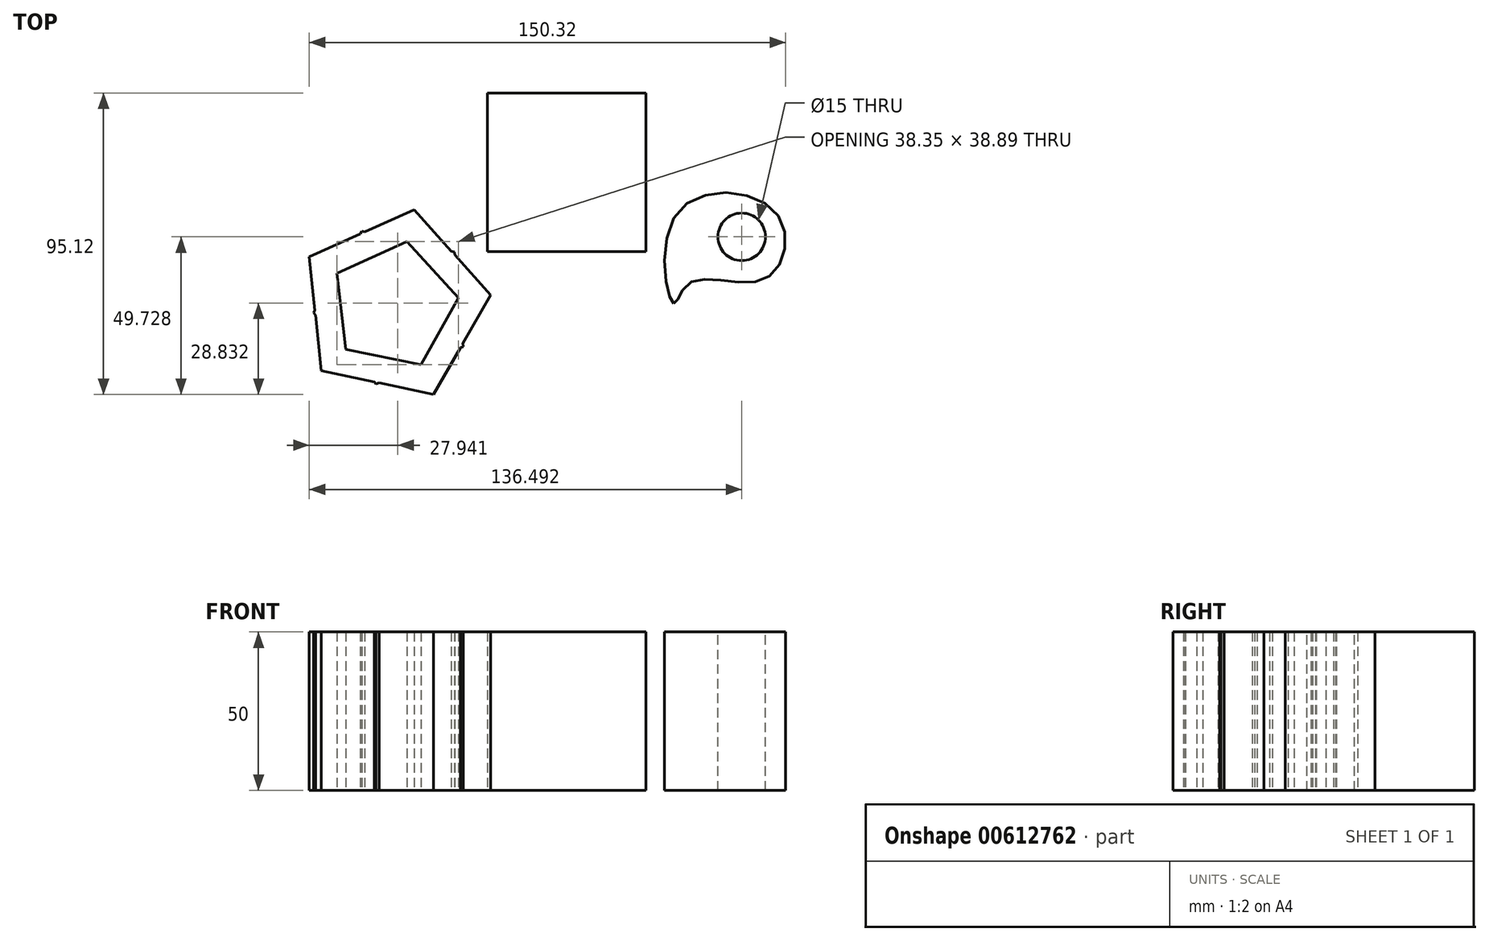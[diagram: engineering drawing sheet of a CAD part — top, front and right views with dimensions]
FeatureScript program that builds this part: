
annotation { "Feature Type Name" : "Feature", "Feature Type Description" : "" }
export const myFeature = defineFeature(function(context is Context, id is Id, definition is map)
    precondition{}
    {
        {
            var Q0;
            Q0=qCreatedBy(makeId("Top.planeOp"),FACE);
            var sketch = newSketch(context, id + "F0", { "sketchPlane" : qUnion([Q0])});
            skLineSegment(sketch, "E0.bottom", {"start": v(-25, -25) * mm, "end": v(25, -25) * mm});
            skLineSegment(sketch, "E0.top", {"start": v(-25, 25) * mm, "end": v(25, 25) * mm});
            skLineSegment(sketch, "E0.left", {"start": v(-25, -25) * mm, "end": v(-25, 25) * mm});
            skLineSegment(sketch, "E0.right", {"start": v(25, -25) * mm, "end": v(25, 25) * mm});
            skPoint(sketch, "E0.middle", {"position": v(0, 0) * mm});
            skSolve(sketch);
        }
        {
            var Q0;
            Q0 = qSketchRegion(id + "F0", true);
            extrude(context, id + "F1", {"entities" : qUnion([Q0]), "depth" : 50 * mm, "offsetDistance" : 25 * mm});
        }
        {
            var Q0;
            Q0=qCreatedBy(makeId("Top.planeOp"),FACE);
            var sketch = newSketch(context, id + "F2", { "sketchPlane" : qUnion([Q0])});
            skFitSpline(sketch, "E1", {"points": [v(33.74, -41.44) * mm, v(34.68, -13.06) * mm, v(66.06, -12.87) * mm, v(62.68, -33.55) * mm, v(38.81, -34.86) * mm, v(33.74, -41.44) * mm]});
            skCircle(sketch, "E2.cCircle", {"center": v(-54.6, -42) * mm, "radius": 24.9 * mm, "construction": true});
            skLineSegment(sketch, "E2.0", {"start": v(-81.27, -26.64) * mm, "end": v(-48.23, -11.9) * mm});
            skLineSegment(sketch, "E2.1", {"start": v(-48.23, -11.9) * mm, "end": v(-23.99, -38.76) * mm});
            skLineSegment(sketch, "E2.2", {"start": v(-23.99, -38.76) * mm, "end": v(-42.05, -70.12) * mm});
            skLineSegment(sketch, "E2.3", {"start": v(-42.05, -70.12) * mm, "end": v(-77.46, -62.62) * mm});
            skLineSegment(sketch, "E2.4", {"start": v(-77.46, -62.62) * mm, "end": v(-81.27, -26.64) * mm});
            skPoint(sketch, "E2.0.midPoint", {"position": v(-64.75, -19.26) * mm});
            skCircle(sketch, "E3.cCircle", {"center": v(-54.6, -42) * mm, "radius": 20.61 * mm, "construction": true});
            skLineSegment(sketch, "E3.0", {"start": v(-64.7, -18.62) * mm, "end": v(-35.48, -25.17) * mm});
            skLineSegment(sketch, "E3.1", {"start": v(-35.48, -25.17) * mm, "end": v(-32.68, -55) * mm});
            skLineSegment(sketch, "E3.2", {"start": v(-32.68, -55) * mm, "end": v(-60.17, -66.86) * mm});
            skLineSegment(sketch, "E3.3", {"start": v(-60.17, -66.86) * mm, "end": v(-79.96, -44.39) * mm});
            skLineSegment(sketch, "E3.4", {"start": v(-79.96, -44.39) * mm, "end": v(-64.7, -18.62) * mm});
            skPoint(sketch, "E3.0.midPoint", {"position": v(-50.09, -21.9) * mm});
            skCircle(sketch, "E4.cCircle", {"center": v(-54.6, -42) * mm, "radius": 16.65 * mm, "construction": true});
            skLineSegment(sketch, "E4.0", {"start": v(-69.77, -55.9) * mm, "end": v(-72.5, -31.87) * mm});
            skLineSegment(sketch, "E4.1", {"start": v(-72.5, -31.87) * mm, "end": v(-50.5, -21.85) * mm});
            skLineSegment(sketch, "E4.2", {"start": v(-50.5, -21.85) * mm, "end": v(-34.15, -39.68) * mm});
            skLineSegment(sketch, "E4.3", {"start": v(-34.15, -39.68) * mm, "end": v(-46.07, -60.73) * mm});
            skLineSegment(sketch, "E4.4", {"start": v(-46.07, -60.73) * mm, "end": v(-69.77, -55.9) * mm});
            skPoint(sketch, "E4.0.midPoint", {"position": v(-71.14, -43.89) * mm});
            skSolve(sketch);
        }
        {
            var Q0;
            Q0=makeQuery(id+"F2.imprint","IMPRINT",FACE,{"disambiguationData":[TD([[makeQuery(id+"F2.imprint","IMPRINT",EDGE,{"derivedFrom":sQuery(id+"F2.wireOp",EDGE,"E1")}),-1.0]])]});
            var Q1;
            {var subQ0=sQuery(id+"F2.wireOp",EDGE,"E2.4");var subQ1=sQuery(id+"F2.wireOp",EDGE,"E2.0");var subQ2=makeQuery(id+"F2.imprint","INTERSECT",VERTEX,{"derivedFrom":[subQ1,subQ0]});Q1=makeQuery(id+"F2.imprint","IMPRINT",FACE,{"disambiguationData":[TD([[makeQuery(id+"F2.imprint","IMPRINT",EDGE,{"disambiguationData":[TD([[subQ2,-1.0]])],"derivedFrom":subQ1}),-1.0]])]});}
            var Q2;
            {var subQ0=sQuery(id+"F2.wireOp",EDGE,"E3.4");var subQ1=sQuery(id+"F2.wireOp",EDGE,"E2.0");var subQ2=makeQuery(id+"F2.imprint","INTERSECT",VERTEX,{"derivedFrom":[subQ1,subQ0]});Q2=makeQuery(id+"F2.imprint","IMPRINT",FACE,{"disambiguationData":[TD([[makeQuery(id+"F2.imprint","IMPRINT",EDGE,{"disambiguationData":[TD([[subQ2,-1.0]])],"derivedFrom":subQ1}),1.0]])]});}
            var Q3;
            {var subQ0=sQuery(id+"F2.wireOp",EDGE,"E3.0");var subQ1=sQuery(id+"F2.wireOp",EDGE,"E2.1");var subQ2=makeQuery(id+"F2.imprint","INTERSECT",VERTEX,{"derivedFrom":[subQ1,subQ0]});Q3=makeQuery(id+"F2.imprint","IMPRINT",FACE,{"disambiguationData":[TD([[makeQuery(id+"F2.imprint","IMPRINT",EDGE,{"disambiguationData":[TD([[subQ2,-1.0]])],"derivedFrom":subQ1}),1.0]])]});}
            var Q4;
            {var subQ0=sQuery(id+"F2.wireOp",EDGE,"E2.2");var subQ1=sQuery(id+"F2.wireOp",EDGE,"E2.1");var subQ2=makeQuery(id+"F2.imprint","INTERSECT",VERTEX,{"derivedFrom":[subQ1,subQ0]});Q4=makeQuery(id+"F2.imprint","IMPRINT",FACE,{"disambiguationData":[TD([[makeQuery(id+"F2.imprint","IMPRINT",EDGE,{"disambiguationData":[TD([[subQ2,1.0]])],"derivedFrom":subQ1}),-1.0]])]});}
            var Q5;
            {var subQ0=sQuery(id+"F2.wireOp",EDGE,"E3.1");var subQ1=sQuery(id+"F2.wireOp",EDGE,"E2.2");var subQ2=makeQuery(id+"F2.imprint","INTERSECT",VERTEX,{"derivedFrom":[subQ1,subQ0]});Q5=makeQuery(id+"F2.imprint","IMPRINT",FACE,{"disambiguationData":[TD([[makeQuery(id+"F2.imprint","IMPRINT",EDGE,{"disambiguationData":[TD([[subQ2,-1.0]])],"derivedFrom":subQ1}),1.0]])]});}
            var Q6;
            {var subQ0=sQuery(id+"F2.wireOp",EDGE,"E2.3");var subQ1=sQuery(id+"F2.wireOp",EDGE,"E2.2");var subQ2=makeQuery(id+"F2.imprint","INTERSECT",VERTEX,{"derivedFrom":[subQ1,subQ0]});Q6=makeQuery(id+"F2.imprint","IMPRINT",FACE,{"disambiguationData":[TD([[makeQuery(id+"F2.imprint","IMPRINT",EDGE,{"disambiguationData":[TD([[subQ2,1.0]])],"derivedFrom":subQ1}),-1.0]])]});}
            var Q7;
            {var subQ0=sQuery(id+"F2.wireOp",EDGE,"E3.2");var subQ1=sQuery(id+"F2.wireOp",EDGE,"E2.3");var subQ2=makeQuery(id+"F2.imprint","INTERSECT",VERTEX,{"derivedFrom":[subQ1,subQ0]});Q7=makeQuery(id+"F2.imprint","IMPRINT",FACE,{"disambiguationData":[TD([[makeQuery(id+"F2.imprint","IMPRINT",EDGE,{"disambiguationData":[TD([[subQ2,-1.0]])],"derivedFrom":subQ1}),1.0]])]});}
            var Q8;
            {var subQ0=sQuery(id+"F2.wireOp",EDGE,"E2.4");var subQ1=sQuery(id+"F2.wireOp",EDGE,"E2.3");var subQ2=makeQuery(id+"F2.imprint","INTERSECT",VERTEX,{"derivedFrom":[subQ1,subQ0]});Q8=makeQuery(id+"F2.imprint","IMPRINT",FACE,{"disambiguationData":[TD([[makeQuery(id+"F2.imprint","IMPRINT",EDGE,{"disambiguationData":[TD([[subQ2,1.0]])],"derivedFrom":subQ1}),-1.0]])]});}
            var Q9;
            {var subQ0=sQuery(id+"F2.wireOp",EDGE,"E3.3");var subQ1=sQuery(id+"F2.wireOp",EDGE,"E2.4");var subQ2=makeQuery(id+"F2.imprint","INTERSECT",VERTEX,{"derivedFrom":[subQ1,subQ0]});Q9=makeQuery(id+"F2.imprint","IMPRINT",FACE,{"disambiguationData":[TD([[makeQuery(id+"F2.imprint","IMPRINT",EDGE,{"disambiguationData":[TD([[subQ2,-1.0]])],"derivedFrom":subQ1}),1.0]])]});}
            var Q10;
            Q10=makeQuery(id+"F2.imprint","IMPRINT",FACE,{"disambiguationData":[TD([[makeQuery(id+"F2.imprint","IMPRINT",EDGE,{"derivedFrom":sQuery(id+"F2.wireOp",EDGE,"E4.0")}),1.0]])]});
            var Q11;
            {var subQ0=sQuery(id+"F2.wireOp",EDGE,"E2.1");var subQ1=sQuery(id+"F2.wireOp",EDGE,"E2.0");var subQ2=makeQuery(id+"F2.imprint","INTERSECT",VERTEX,{"derivedFrom":[subQ1,subQ0]});Q11=makeQuery(id+"F2.imprint","IMPRINT",FACE,{"disambiguationData":[TD([[makeQuery(id+"F2.imprint","IMPRINT",EDGE,{"disambiguationData":[TD([[subQ2,1.0]])],"derivedFrom":subQ1}),-1.0]])]});}
            extrude(context, id + "F3", {"entities" : qUnion([Q0, Q1, Q2, Q3, Q4, Q5, Q6, Q7, Q8, Q9, Q10, Q11]), "depth" : 50 * mm, "offsetDistance" : 25 * mm});
        }
        {
            var Q0;
            Q0=makeQuery(id+"F3.opExtrude","CAP_FACE",FACE,{"disambiguationData":[OSD([sQuery(id+"F2.wireOp",EDGE,"E1")])],"isStart":false});
            var sketch = newSketch(context, id + "F4", { "sketchPlane" : qUnion([Q0])});
            skCircle(sketch, "E5", {"center": v(55.22, -20.4) * mm, "radius": 7.5 * mm});
            skSolve(sketch);
        }
        {
            var Q0;
            Q0 = qSketchRegion(id + "F4", true);
            extrude(context, id + "F5", {"entities" : qUnion([Q0]), "operationType" : NewBodyOperationType.REMOVE, "oppositeDirection" : true, "depth" : 50 * mm, "offsetDistance" : 25 * mm});
        }
    });
